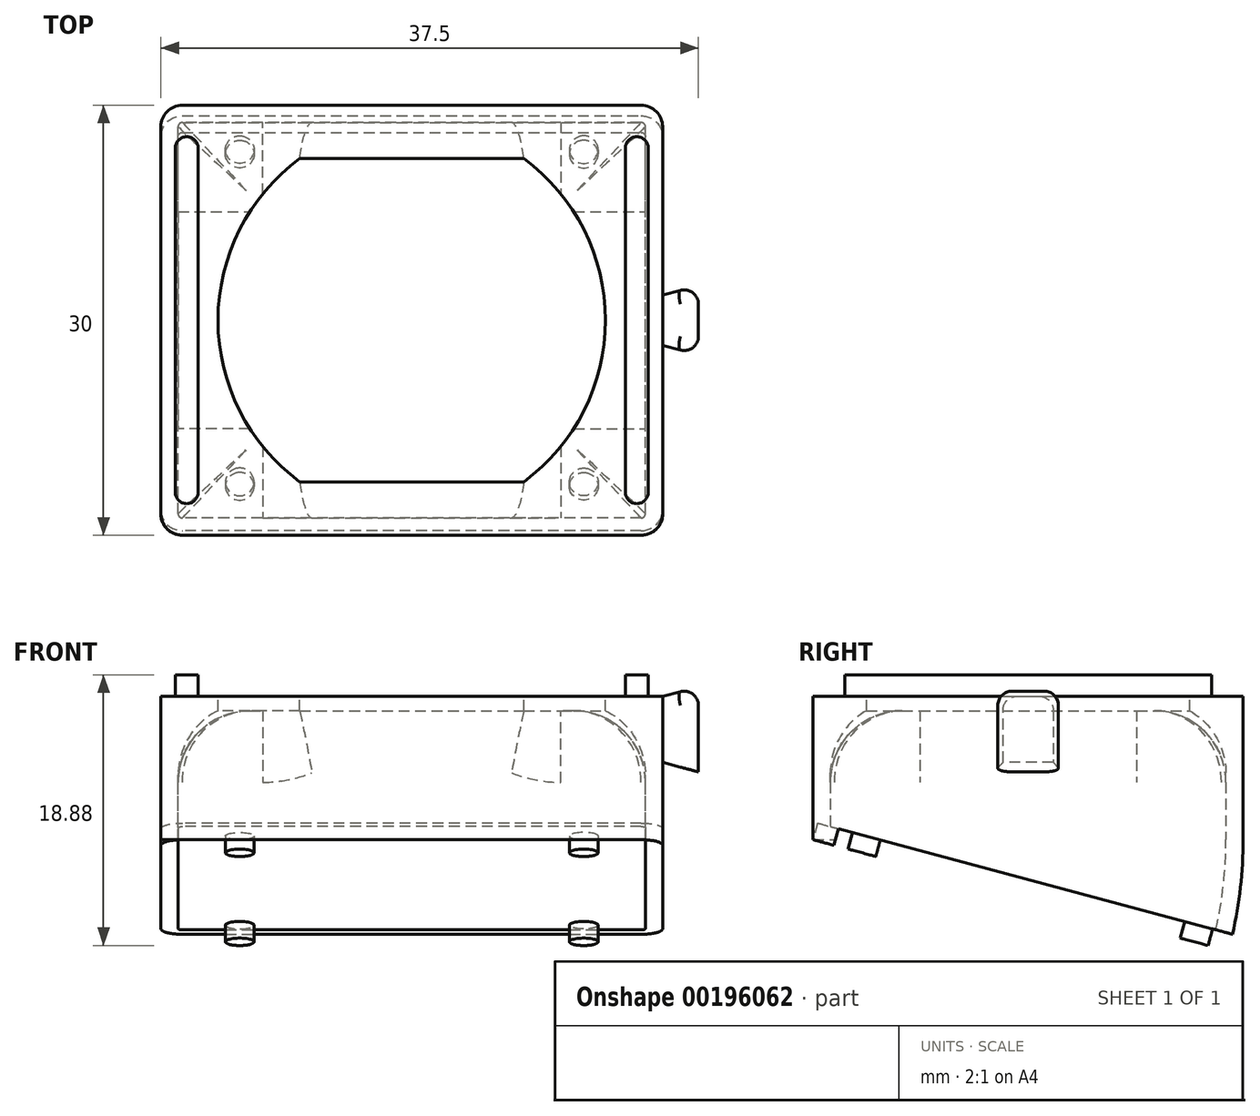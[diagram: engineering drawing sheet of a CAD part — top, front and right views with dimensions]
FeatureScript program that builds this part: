
annotation { "Feature Type Name" : "Feature", "Feature Type Description" : "" }
export const myFeature = defineFeature(function(context is Context, id is Id, definition is map)
    precondition{}
    {
        {
            var Q0;
            Q0=qCreatedBy(makeId("Top.planeOp"),FACE);
            var sketch = newSketch(context, id + "F0", { "sketchPlane" : qUnion([Q0])});
            skLineSegment(sketch, "E0.bottom", {"start": v(17.5, -15) * mm, "end": v(-17.5, -15) * mm});
            skLineSegment(sketch, "E0.top", {"start": v(17.5, 15) * mm, "end": v(-17.5, 15) * mm});
            skLineSegment(sketch, "E0.left", {"start": v(17.5, -15) * mm, "end": v(17.5, 15) * mm});
            skLineSegment(sketch, "E0.right", {"start": v(-17.5, -15) * mm, "end": v(-17.5, 15) * mm});
            skPoint(sketch, "E0.middle", {"position": v(0, 0) * mm});
            skSolve(sketch);
        }
        {
            var Q0;
            Q0 = qSketchRegion(id + "F0", true);
            extrude(context, id + "F1", {"entities" : qUnion([Q0]), "depth" : 10 * mm});
        }
        {
            var Q0;
            Q0=makeQuery(id+"F1.opExtrude","SWEPT_EDGE",EDGE,{"disambiguationData":[OSD([sQuery(id+"F0.wireOp",EDGE,"E0.top"),sQuery(id+"F0.wireOp",EDGE,"E0.left")])]});
            var Q1;
            Q1=makeQuery(id+"F1.opExtrude","SWEPT_EDGE",EDGE,{"disambiguationData":[OSD([sQuery(id+"F0.wireOp",EDGE,"E0.top"),sQuery(id+"F0.wireOp",EDGE,"E0.right")])]});
            var Q2;
            Q2=makeQuery(id+"F1.opExtrude","SWEPT_EDGE",EDGE,{"disambiguationData":[OSD([sQuery(id+"F0.wireOp",EDGE,"E0.bottom"),sQuery(id+"F0.wireOp",EDGE,"E0.right")])]});
            var Q3;
            Q3=makeQuery(id+"F1.opExtrude","SWEPT_EDGE",EDGE,{"disambiguationData":[OSD([sQuery(id+"F0.wireOp",EDGE,"E0.bottom"),sQuery(id+"F0.wireOp",EDGE,"E0.left")])]});
            fillet(context, id + "F2", {"entities" : qUnion([Q0, Q1, Q2, Q3]), "radius" : 1.5 * mm, "tangentPropagation" : true, "allowEdgeOverflow" : false});
        }
        {
            var Q0;
            Q0=makeQuery(id+"F1.opExtrude","CAP_FACE",FACE,{"disambiguationData":[OSD([sQuery(id+"F0.wireOp",EDGE,"E0.bottom"),sQuery(id+"F0.wireOp",EDGE,"E0.top"),sQuery(id+"F0.wireOp",EDGE,"E0.left"),sQuery(id+"F0.wireOp",EDGE,"E0.right")])],"isStart":true});
            var Q1;
            Q1=makeQuery(id+"F1.opExtrude","CAP_EDGE",EDGE,{"disambiguationData":[OSD([sQuery(id+"F0.wireOp",EDGE,"E0.bottom")])],"isStart":true});
            revolve(context, id + "F3", {"operationType" : NewBodyOperationType.ADD, "entities" : qUnion([Q0]), "axis" : qUnion([Q1]), "revolveType" : RevolveType.ONE_DIRECTION, "angle" : 15 * degree});
        }
        {
            var Q0;
            Q0=makeQuery(id+"F1.opExtrude","CAP_FACE",FACE,{"disambiguationData":[OSD([sQuery(id+"F0.wireOp",EDGE,"E0.bottom"),sQuery(id+"F0.wireOp",EDGE,"E0.top"),sQuery(id+"F0.wireOp",EDGE,"E0.left"),sQuery(id+"F0.wireOp",EDGE,"E0.right")])],"isStart":false});
            shell(context, id + "F4", {"entities" : qUnion([Q0]), "thickness" : 1.2 * mm});
        }
        {
            var Q0;
            Q0=makeQuery(id+"F3.opRevolve","CAP_FACE",FACE,{"disambiguationData":[OSD([sQuery(id+"F0.wireOp",EDGE,"E0.bottom"),sQuery(id+"F0.wireOp",EDGE,"E0.top"),sQuery(id+"F0.wireOp",EDGE,"E0.left"),sQuery(id+"F0.wireOp",EDGE,"E0.right")])],"isStart":false});
            var sketch = newSketch(context, id + "F5", { "sketchPlane" : qUnion([Q0])});
            skCircle(sketch, "E1", {"center": v(0, 0) * mm, "radius": 13.5 * mm});
            skCircle(sketch, "E2", {"center": v(12, -13.04) * mm, "radius": 1 * mm});
            skCircle(sketch, "E3.MirrorC", {"center": v(-12, -13.04) * mm, "radius": 1 * mm});
            skCircle(sketch, "E4.MirrorC", {"center": v(-12, 10.96) * mm, "radius": 1 * mm});
            skCircle(sketch, "E5.MirrorC", {"center": v(12, 10.96) * mm, "radius": 1 * mm});
            skSolve(sketch);
        }
        {
            var Q0;
            Q0=makeQuery(id+"F5.imprint","IMPRINT",FACE,{"disambiguationData":[TD([[makeQuery(id+"F5.imprint","IMPRINT",EDGE,{"derivedFrom":sQuery(id+"F5.wireOp",EDGE,"E1")}),1.0]])]});
            var Q1;
            Q1=makeQuery(id+"F5.imprint","IMPRINT",FACE,{"disambiguationData":[TD([[makeQuery(id+"F5.imprint","IMPRINT",EDGE,{"derivedFrom":sQuery(id+"F5.wireOp",EDGE,"E3.MirrorC")}),-1.0]])]});
            var Q2;
            Q2=makeQuery(id+"F5.imprint","IMPRINT",FACE,{"disambiguationData":[TD([[makeQuery(id+"F5.imprint","IMPRINT",EDGE,{"derivedFrom":sQuery(id+"F5.wireOp",EDGE,"E2")}),1.0]])]});
            var Q3;
            Q3=makeQuery(id+"F5.imprint","IMPRINT",FACE,{"disambiguationData":[TD([[makeQuery(id+"F5.imprint","IMPRINT",EDGE,{"derivedFrom":sQuery(id+"F5.wireOp",EDGE,"E5.MirrorC")}),-1.0]])]});
            var Q4;
            Q4=makeQuery(id+"F5.imprint","IMPRINT",FACE,{"disambiguationData":[TD([[makeQuery(id+"F5.imprint","IMPRINT",EDGE,{"derivedFrom":sQuery(id+"F5.wireOp",EDGE,"E4.MirrorC")}),1.0]])]});
            extrude(context, id + "F6", {"entities" : qUnion([Q0, Q1, Q2, Q3, Q4]), "operationType" : NewBodyOperationType.REMOVE, "oppositeDirection" : true, "depth" : 1.2 * mm});
        }
        {
            var Q0;
            Q0=makeQuery(id+"F1.opExtrude","CAP_FACE",FACE,{"disambiguationData":[OSD([sQuery(id+"F0.wireOp",EDGE,"E0.bottom"),sQuery(id+"F0.wireOp",EDGE,"E0.top"),sQuery(id+"F0.wireOp",EDGE,"E0.left"),sQuery(id+"F0.wireOp",EDGE,"E0.right")])],"isStart":false});
            var sketch = newSketch(context, id + "F7", { "sketchPlane" : qUnion([Q0])});
            skLineSegment(sketch, "E6.bottom", {"start": v(16.34, 13.8) * mm, "end": v(-16.34, 13.8) * mm});
            skLineSegment(sketch, "E6.top", {"start": v(16.34, -13.8) * mm, "end": v(-16.34, -13.8) * mm});
            skLineSegment(sketch, "E6.left", {"start": v(16.34, 13.8) * mm, "end": v(16.34, -13.8) * mm});
            skLineSegment(sketch, "E6.right", {"start": v(-16.34, 13.8) * mm, "end": v(-16.34, -13.8) * mm});
            skPoint(sketch, "E6.middle", {"position": v(0, 0) * mm});
            skLineSegment(sketch, "E7", {"start": v(-16.3, 11.28) * mm, "end": v(16.34, 11.28) * mm});
            skLineSegment(sketch, "E8.MirrorCS", {"start": v(-16.3, -11.28) * mm, "end": v(16.34, -11.28) * mm});
            skArc(sketch, "E9", {"start": v(-7.82, 11.28) * mm, "mid": v(-13.52, 0) * mm, "end": v(-7.82, -11.28) * mm});
            skArc(sketch, "E10.MirrorCS", {"start": v(7.82, 11.28) * mm, "mid": v(13.52, 0) * mm, "end": v(7.82, -11.28) * mm});
            skSolve(sketch);
        }
        {
            var Q0;
            Q0 = qSketchRegion(id + "F7", true);
            extrude(context, id + "F8", {"entities" : qUnion([Q0]), "operationType" : NewBodyOperationType.ADD, "oppositeDirection" : true, "depth" : 1 * mm});
        }
        {
            var Q0;
            Q0=makeQuery(id+"F8.opExtrude","CAP_EDGE",EDGE,{"disambiguationData":[OSD([sQuery(id+"F7.wireOp",EDGE,"E6.bottom")])],"isStart":false});
            var Q1;
            Q1=makeQuery(id+"F8.boolean.opBoolean","INTERSECT",EDGE,{"derivedFrom":[makeQuery(id+"F4.opShell","OFFSET_FACE",FACE,{"disambiguationData":[OSD([sQuery(id+"F0.wireOp",EDGE,"E0.right")])]}),makeQuery(id+"F8.opExtrude","CAP_FACE",FACE,{"disambiguationData":[OSD([sQuery(id+"F7.wireOp",EDGE,"E6.bottom"),sQuery(id+"F7.wireOp",EDGE,"E6.top"),sQuery(id+"F7.wireOp",EDGE,"E6.left"),sQuery(id+"F7.wireOp",EDGE,"E6.right"),sQuery(id+"F7.wireOp",EDGE,"E7"),sQuery(id+"F7.wireOp",EDGE,"E8.MirrorCS"),sQuery(id+"F7.wireOp",EDGE,"E9"),sQuery(id+"F7.wireOp",EDGE,"E10.MirrorCS")])],"isStart":false})]});
            var Q2;
            Q2=makeQuery(id+"F8.boolean.opBoolean","INTERSECT",EDGE,{"derivedFrom":[makeQuery(id+"F4.opShell","OFFSET_FACE",FACE,{"disambiguationData":[OSD([sQuery(id+"F0.wireOp",EDGE,"E0.left")])]}),makeQuery(id+"F8.opExtrude","CAP_FACE",FACE,{"disambiguationData":[OSD([sQuery(id+"F7.wireOp",EDGE,"E6.bottom"),sQuery(id+"F7.wireOp",EDGE,"E6.top"),sQuery(id+"F7.wireOp",EDGE,"E6.left"),sQuery(id+"F7.wireOp",EDGE,"E6.right"),sQuery(id+"F7.wireOp",EDGE,"E7"),sQuery(id+"F7.wireOp",EDGE,"E8.MirrorCS"),sQuery(id+"F7.wireOp",EDGE,"E9"),sQuery(id+"F7.wireOp",EDGE,"E10.MirrorCS")])],"isStart":false})]});
            var Q3;
            Q3=makeQuery(id+"F8.opExtrude","CAP_EDGE",EDGE,{"disambiguationData":[OSD([sQuery(id+"F7.wireOp",EDGE,"E6.top")])],"isStart":false});
            fillet(context, id + "F9", {"entities" : qUnion([Q0, Q1, Q2, Q3]), "radius" : 5 * mm, "tangentPropagation" : true, "allowEdgeOverflow" : false});
        }
        {
            var Q0;
            Q0=makeQuery(id+"F8.boolean.opBoolean","MERGE",FACE,{"derivedFrom":[makeQuery(id+"F1.opExtrude","CAP_FACE",FACE,{"disambiguationData":[OSD([sQuery(id+"F0.wireOp",EDGE,"E0.bottom"),sQuery(id+"F0.wireOp",EDGE,"E0.top"),sQuery(id+"F0.wireOp",EDGE,"E0.left"),sQuery(id+"F0.wireOp",EDGE,"E0.right")])],"isStart":false}),makeQuery(id+"F8.opExtrude","CAP_FACE",FACE,{"disambiguationData":[OSD([sQuery(id+"F7.wireOp",EDGE,"E6.bottom"),sQuery(id+"F7.wireOp",EDGE,"E6.top"),sQuery(id+"F7.wireOp",EDGE,"E6.left"),sQuery(id+"F7.wireOp",EDGE,"E6.right"),sQuery(id+"F7.wireOp",EDGE,"E7"),sQuery(id+"F7.wireOp",EDGE,"E8.MirrorCS"),sQuery(id+"F7.wireOp",EDGE,"E9"),sQuery(id+"F7.wireOp",EDGE,"E10.MirrorCS")])],"isStart":true})]});
            var sketch = newSketch(context, id + "F10", { "sketchPlane" : qUnion([Q0])});
            skLineSegment(sketch, "E11.bottom", {"start": v(-14.9, -12) * mm, "end": v(-16.5, -12) * mm});
            skLineSegment(sketch, "E11.top", {"start": v(-14.9, 12) * mm, "end": v(-16.5, 12) * mm});
            skLineSegment(sketch, "E11.left", {"start": v(-14.9, -12) * mm, "end": v(-14.9, 12) * mm});
            skLineSegment(sketch, "E11.right", {"start": v(-16.5, -12) * mm, "end": v(-16.5, 12) * mm});
            skPoint(sketch, "E11.middle", {"position": v(-15.7, 0) * mm});
            skLineSegment(sketch, "E12.MirrorCS", {"start": v(14.9, -12) * mm, "end": v(14.9, 12) * mm});
            skLineSegment(sketch, "E13.MirrorCS", {"start": v(14.9, 12) * mm, "end": v(16.5, 12) * mm});
            skLineSegment(sketch, "E14.MirrorCS", {"start": v(14.9, -12) * mm, "end": v(16.5, -12) * mm});
            skLineSegment(sketch, "E15.MirrorCS", {"start": v(16.5, -12) * mm, "end": v(16.5, 12) * mm});
            skArc(sketch, "E16", {"start": v(-14.9, 12) * mm, "mid": v(-15.7, 12.8) * mm, "end": v(-16.5, 12) * mm});
            skArc(sketch, "E17.MirrorCS", {"start": v(-14.9, -12) * mm, "mid": v(-15.7, -12.8) * mm, "end": v(-16.5, -12) * mm});
            skArc(sketch, "E18.MirrorCS", {"start": v(14.9, 12) * mm, "mid": v(15.7, 12.8) * mm, "end": v(16.5, 12) * mm});
            skArc(sketch, "E19.MirrorCS", {"start": v(14.9, -12) * mm, "mid": v(15.7, -12.8) * mm, "end": v(16.5, -12) * mm});
            skSolve(sketch);
        }
        {
            var Q0;
            Q0 = qSketchRegion(id + "F10", true);
            extrude(context, id + "F11", {"entities" : qUnion([Q0]), "operationType" : NewBodyOperationType.ADD, "depth" : 1.5 * mm});
        }
        {
            var Q0;
            Q0=makeQuery(id+"F1.opExtrude","SWEPT_FACE",FACE,{"disambiguationData":[OSD([sQuery(id+"F0.wireOp",EDGE,"E0.left")])]});
            var sketch = newSketch(context, id + "F12", { "sketchPlane" : qUnion([Q0])});
            skLineSegment(sketch, "E20.bottom", {"start": v(-1.75, 5.4) * mm, "end": v(1.75, 5.4) * mm});
            skLineSegment(sketch, "E20.top", {"start": v(-1.75, 10) * mm, "end": v(1.75, 10) * mm});
            skLineSegment(sketch, "E20.left", {"start": v(-1.75, 5.4) * mm, "end": v(-1.75, 10) * mm});
            skLineSegment(sketch, "E20.right", {"start": v(1.75, 5.4) * mm, "end": v(1.75, 10) * mm});
            skPoint(sketch, "E20.middle", {"position": v(0, 7.7) * mm});
            skSolve(sketch);
        }
        {
            var Q0;
            Q0 = qSketchRegion(id + "F12", true);
            extrude(context, id + "F13", {"entities" : qUnion([Q0]), "operationType" : NewBodyOperationType.ADD, "depth" : 2.5 * mm, "hasDraft" : true, "draftAngle" : 15 * degree});
        }
        {
            var Q0;
            Q0=makeQuery(id+"F13.opExtrude","CAP_EDGE",EDGE,{"disambiguationData":[OSD([sQuery(id+"F12.wireOp",EDGE,"E20.top")])],"isStart":false});
            var Q1;
            Q1=makeQuery(id+"F13.opExtrude","CAP_EDGE",EDGE,{"disambiguationData":[OSD([sQuery(id+"F12.wireOp",EDGE,"E20.left")])],"isStart":false});
            var Q2;
            Q2=makeQuery(id+"F13.opExtrude","CAP_EDGE",EDGE,{"disambiguationData":[OSD([sQuery(id+"F12.wireOp",EDGE,"E20.right")])],"isStart":false});
            var Q3;
            Q3=makeQuery(id+"F13.opExtrude","SWEPT_EDGE",EDGE,{"disambiguationData":[OSD([sQuery(id+"F0.wireOp",EDGE,"E0.left"),sQuery(id+"F12.wireOp",EDGE,"E20.top"),sQuery(id+"F12.wireOp",EDGE,"E20.left")])]});
            var Q4;
            Q4=makeQuery(id+"F13.opExtrude","SWEPT_EDGE",EDGE,{"disambiguationData":[OSD([sQuery(id+"F0.wireOp",EDGE,"E0.left"),sQuery(id+"F12.wireOp",EDGE,"E20.top"),sQuery(id+"F12.wireOp",EDGE,"E20.right")])]});
            fillet(context, id + "F14", {"entities" : qUnion([Q0, Q1, Q2, Q3, Q4]), "radius" : 1 * mm, "tangentPropagation" : true, "allowEdgeOverflow" : false});
        }
        {
            var Q0;
            Q0=makeQuery(id+"F1.opExtrude","SWEPT_BODY",BODY,{"disambiguationData":[OSD([sQuery(id+"F0.wireOp",EDGE,"E0.bottom"),sQuery(id+"F0.wireOp",EDGE,"E0.top"),sQuery(id+"F0.wireOp",EDGE,"E0.left"),sQuery(id+"F0.wireOp",EDGE,"E0.right")])]});
            var Q1;
            Q1=qCreatedBy(makeId("Right.planeOp"),FACE);
            mirror(context, id + "F15", {"operationType" : NewBodyOperationType.ADD, "entities" : qUnion([Q0]), "mirrorPlane" : qUnion([Q1])});
        }
    });
